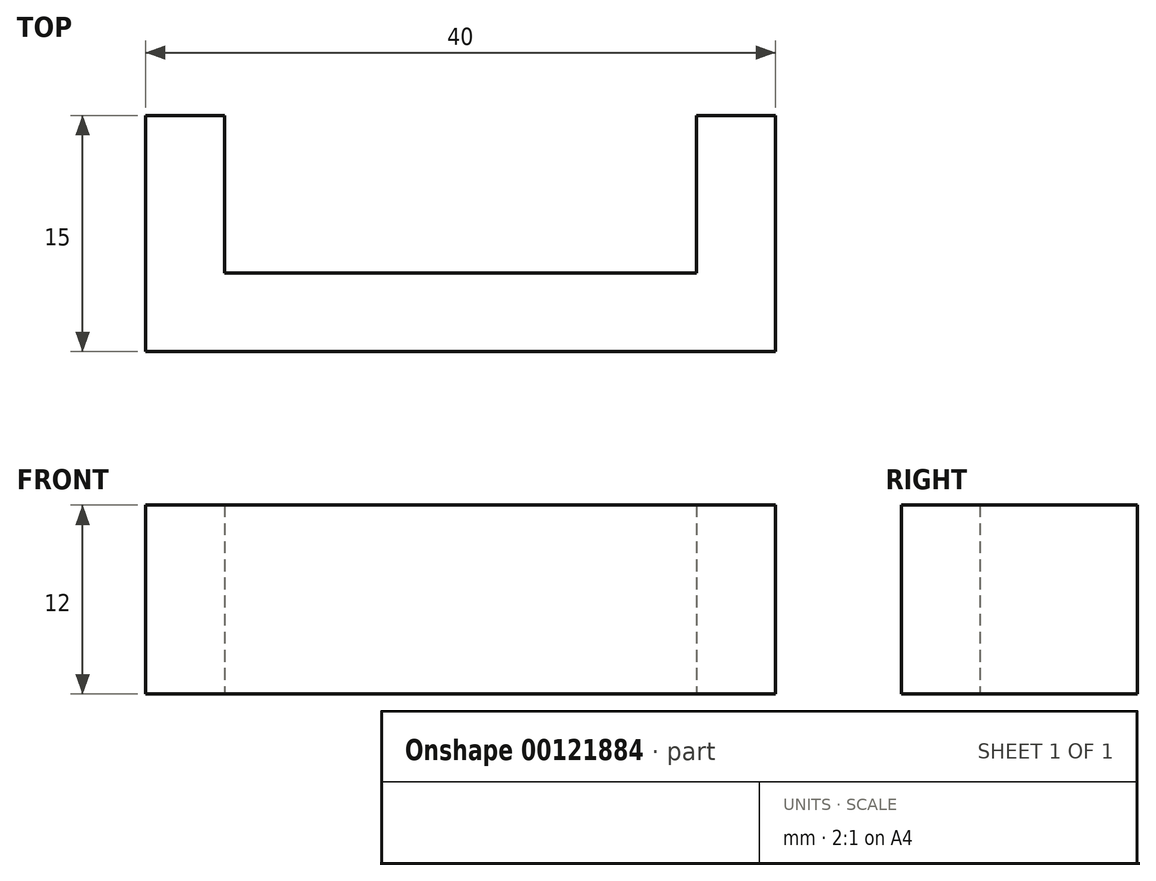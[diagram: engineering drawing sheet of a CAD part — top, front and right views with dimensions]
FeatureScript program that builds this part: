
annotation { "Feature Type Name" : "Feature", "Feature Type Description" : "" }
export const myFeature = defineFeature(function(context is Context, id is Id, definition is map)
    precondition{}
    {
        {
            var Q0;
            Q0=qCreatedBy(makeId("Top.planeOp"),FACE);
            var sketch = newSketch(context, id + "F0", { "sketchPlane" : qUnion([Q0])});
            skLineSegment(sketch, "E0", {"start": v(-20, 10) * mm, "end": v(-20, -5) * mm});
            skLineSegment(sketch, "E1", {"start": v(-20, -5) * mm, "end": v(20, -5) * mm});
            skLineSegment(sketch, "E2", {"start": v(20, -5) * mm, "end": v(20, 10) * mm});
            skLineSegment(sketch, "E3", {"start": v(20, 10) * mm, "end": v(15, 10) * mm});
            skLineSegment(sketch, "E4", {"start": v(15, 10) * mm, "end": v(15, 0) * mm});
            skLineSegment(sketch, "E5", {"start": v(15, 0) * mm, "end": v(-15, 0) * mm});
            skLineSegment(sketch, "E6", {"start": v(-15, 0) * mm, "end": v(-15, 10) * mm});
            skLineSegment(sketch, "E7", {"start": v(-15, 10) * mm, "end": v(-20, 10) * mm});
            skSolve(sketch);
        }
        {
            var Q0;
            Q0 = qSketchRegion(id + "F0", true);
            extrude(context, id + "F1", {"entities" : qUnion([Q0]), "depth" : 12 * mm});
        }
    });
